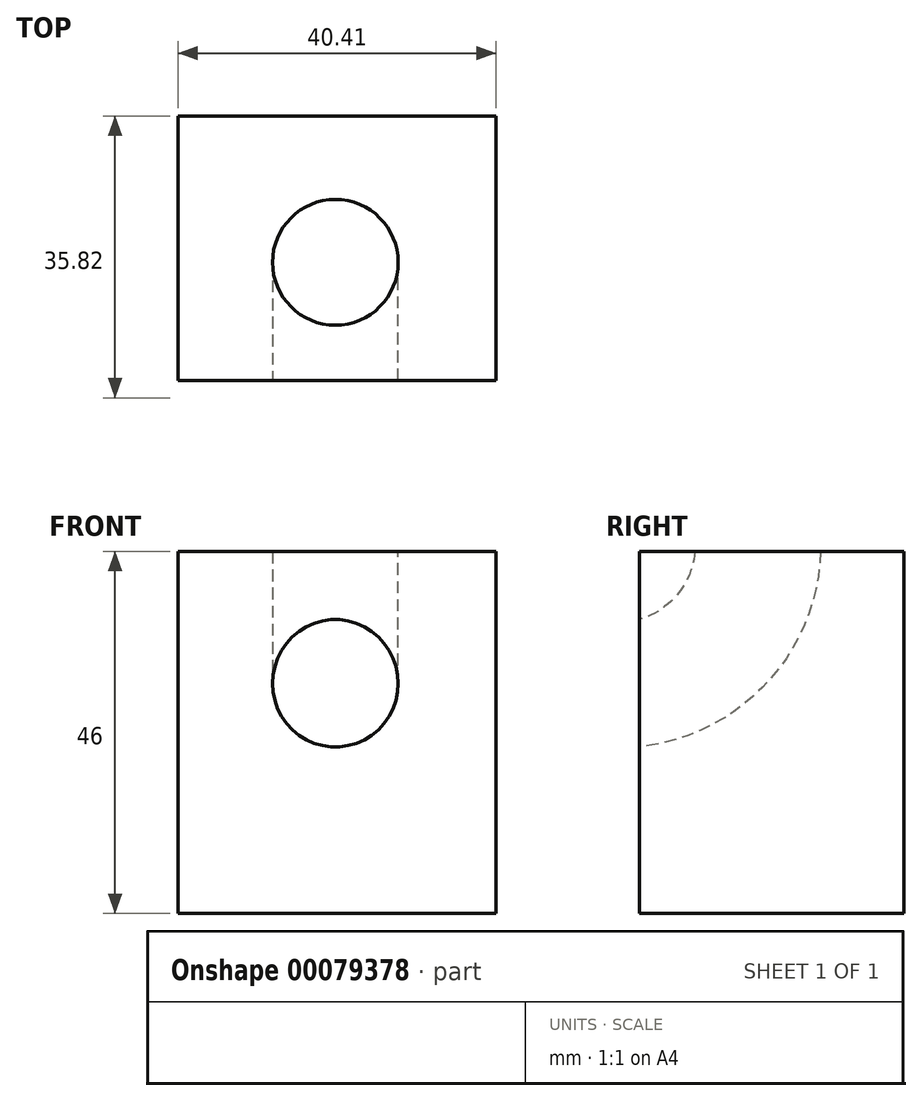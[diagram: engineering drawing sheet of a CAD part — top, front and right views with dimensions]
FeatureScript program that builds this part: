
annotation { "Feature Type Name" : "Feature", "Feature Type Description" : "" }
export const myFeature = defineFeature(function(context is Context, id is Id, definition is map)
    precondition{}
    {
        {
            var Q0;
            Q0=qCreatedBy(makeId("Top.planeOp"),FACE);
            var sketch = newSketch(context, id + "F0", { "sketchPlane" : qUnion([Q0])});
            skLineSegment(sketch, "E0.bottom", {"start": v(-3.92, 0) * mm, "end": v(36.5, 0) * mm});
            skLineSegment(sketch, "E0.top", {"start": v(-3.92, -33.61) * mm, "end": v(36.5, -33.61) * mm});
            skLineSegment(sketch, "E0.left", {"start": v(-3.92, 0) * mm, "end": v(-3.92, -33.61) * mm});
            skLineSegment(sketch, "E0.right", {"start": v(36.5, 0) * mm, "end": v(36.5, -33.61) * mm});
            skSolve(sketch);
        }
        {
            var Q0;
            Q0 = qSketchRegion(id + "F0", true);
            extrude(context, id + "F1", {"entities" : qUnion([Q0]), "depth" : 46 * mm});
        }
        {
            var Q0;
            Q0=makeQuery(id+"F1.opExtrude","CAP_FACE",FACE,{"disambiguationData":[OSD([sQuery(id+"F0.wireOp",EDGE,"E0.bottom"),sQuery(id+"F0.wireOp",EDGE,"E0.top"),sQuery(id+"F0.wireOp",EDGE,"E0.left"),sQuery(id+"F0.wireOp",EDGE,"E0.right")])],"isStart":false});
            var sketch = newSketch(context, id + "F2", { "sketchPlane" : qUnion([Q0])});
            skCircle(sketch, "E1", {"center": v(16.06, -18.6) * mm, "radius": 7.98 * mm});
            skSolve(sketch);
        }
        {
            var Q0;
            Q0=makeQuery(id+"F1.opExtrude","SWEPT_FACE",FACE,{"disambiguationData":[OSD([sQuery(id+"F0.wireOp",EDGE,"E0.right")])]});
            var Q1;
            Q1=sQuery(id+"F2.wireOp",VERTEX,"E1.center");
            cPlane(context, id + "F3", {"entities" : qUnion([Q0, Q1]), "cplaneType" : CPlaneType.PLANE_POINT, "offset" : 150 * mm, "width" : 150 * mm, "height" : 150 * mm});
        }
        {
            var Q0;
            Q0=qCreatedBy(id+"F3.planeOp",FACE);
            var sketch = newSketch(context, id + "F4", { "sketchPlane" : qUnion([Q0])});
            skArc(sketch, "E2", {"start": v(-54.16, 47.6) * mm, "mid": v(-37.18, 29.02) * mm, "end": v(-18.6, 46) * mm});
            skSolve(sketch);
        }
        {
            var Q0;
            Q0=makeQuery(id+"F2.imprint","IMPRINT",FACE,{"disambiguationData":[TD([[makeQuery(id+"F2.imprint","IMPRINT",EDGE,{"derivedFrom":sQuery(id+"F2.wireOp",EDGE,"E1")}),1.0]])]});
            var Q1;
            Q1 = qConstructionFilter(qBodyType(qCreatedBy(id + "F4" ,EDGE), BodyType.WIRE), ConstructionObject.NO);
            sweep(context, id + "F5", {"operationType" : NewBodyOperationType.REMOVE, "profiles" : qUnion([Q0]), "path" : qUnion([Q1])});
        }
    });
